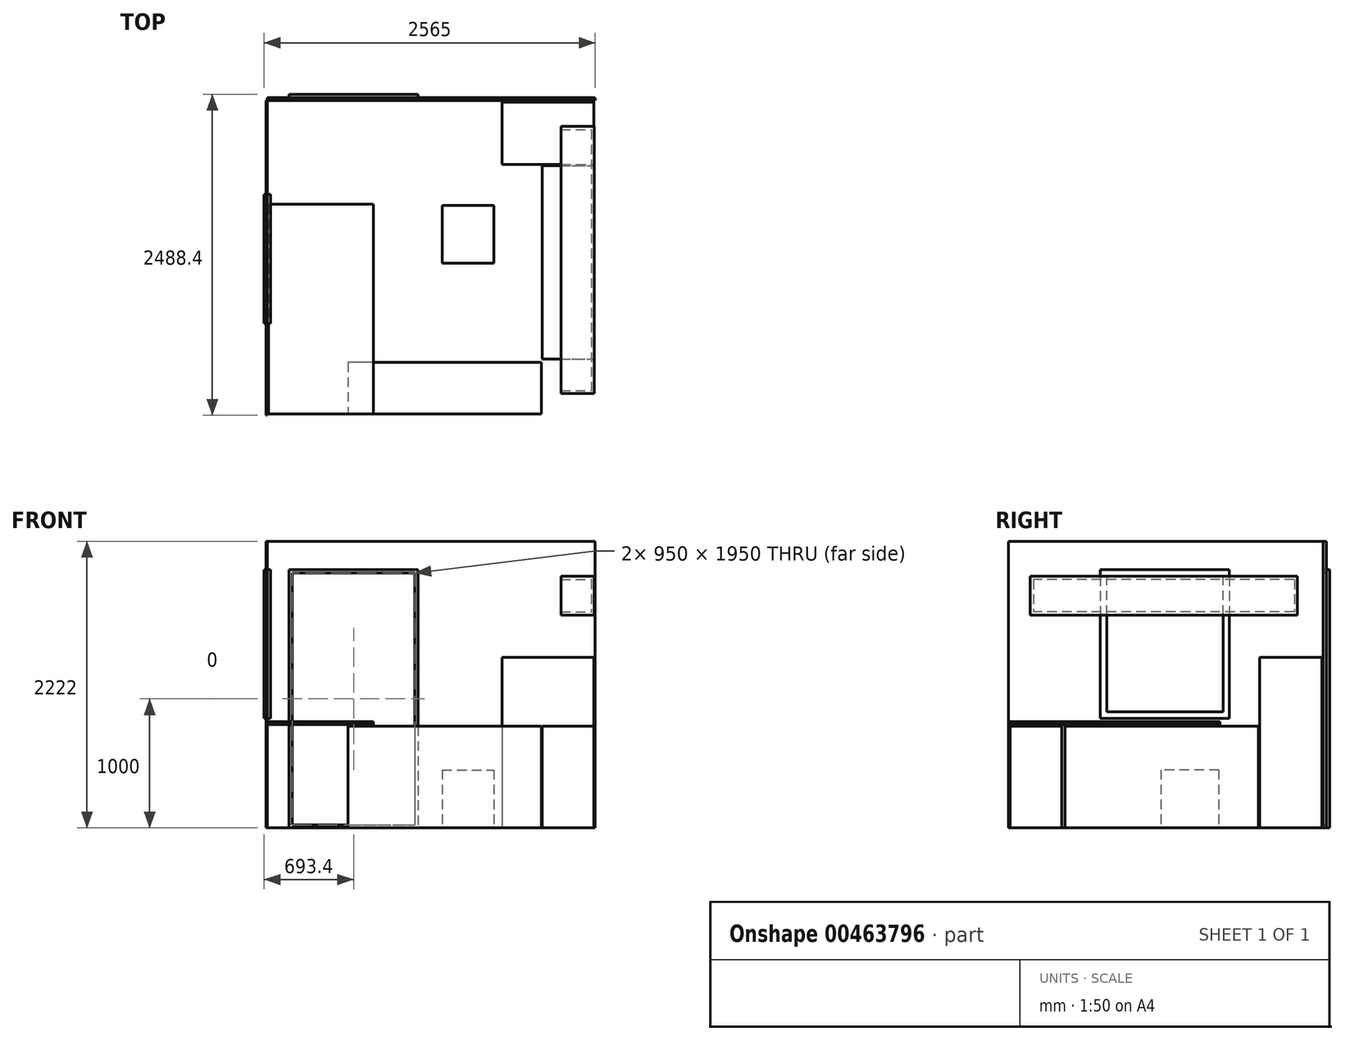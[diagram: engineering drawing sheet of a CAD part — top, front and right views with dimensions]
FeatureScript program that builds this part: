
annotation { "Feature Type Name" : "Feature", "Feature Type Description" : "" }
export const myFeature = defineFeature(function(context is Context, id is Id, definition is map)
    precondition{}
    {
        {
            var Q0;
            Q0=qCreatedBy(makeId("Top.planeOp"),FACE);
            var sketch = newSketch(context, id + "F0", { "sketchPlane" : qUnion([Q0])});
            skLineSegment(sketch, "E0.bottom", {"start": v(0, 0) * mm, "end": v(2540, 0) * mm});
            skLineSegment(sketch, "E0.top", {"start": v(0, 2438.4) * mm, "end": v(2540, 2438.4) * mm});
            skLineSegment(sketch, "E0.left", {"start": v(0, 0) * mm, "end": v(0, 2438.4) * mm});
            skLineSegment(sketch, "E0.right", {"start": v(2540, 0) * mm, "end": v(2540, 2438.4) * mm});
            skSolve(sketch);
        }
        {
            var Q0;
            Q0=qCreatedBy(makeId("Top.planeOp"),FACE);
            cPlane(context, id + "F1", {"entities" : qUnion([Q0]), "cplaneType" : CPlaneType.OFFSET, "offset" : 800 * mm, "width" : 150 * mm, "height" : 150 * mm});
        }
        {
            var Q0;
            Q0=qCreatedBy(makeId("Top.planeOp"),FACE);
            var sketch = newSketch(context, id + "F2", { "sketchPlane" : qUnion([Q0])});
            skLineSegment(sketch, "E1.bottom", {"start": v(1818.8, 2428.4) * mm, "end": v(2530, 2428.4) * mm});
            skLineSegment(sketch, "E1.top", {"start": v(1818.8, 1945.8) * mm, "end": v(2530, 1945.8) * mm});
            skLineSegment(sketch, "E1.left", {"start": v(1818.8, 2428.4) * mm, "end": v(1818.8, 1945.8) * mm});
            skLineSegment(sketch, "E1.right", {"start": v(2530, 2428.4) * mm, "end": v(2530, 1945.8) * mm});
            skSolve(sketch);
        }
        {
            var Q0;
            Q0=qCreatedBy(makeId("Top.planeOp"),FACE);
            var sketch = newSketch(context, id + "F3", { "sketchPlane" : qUnion([Q0])});
            skLineSegment(sketch, "E2.bottom", {"start": v(2130, 1935.8) * mm, "end": v(2530, 1935.8) * mm});
            skLineSegment(sketch, "E2.top", {"start": v(2130, 437.2) * mm, "end": v(2530, 437.2) * mm});
            skLineSegment(sketch, "E2.left", {"start": v(2130, 1935.8) * mm, "end": v(2130, 437.2) * mm});
            skLineSegment(sketch, "E2.right", {"start": v(2530, 1935.8) * mm, "end": v(2530, 437.2) * mm});
            skSolve(sketch);
        }
        {
            var Q0;
            Q0 = qSketchRegion(id + "F3", true);
            extrude(context, id + "F4", {"entities" : qUnion([Q0]), "depth" : (31 * 25.4) * mm});
        }
        {
            var Q0;
            Q0 = qSketchRegion(id + "F2", true);
            extrude(context, id + "F5", {"entities" : qUnion([Q0]), "depth" : 52 * 25.4 * mm});
        }
        {
            var Q0;
            Q0=makeQuery(id+"F0.imprint","IMPRINT",FACE,{"disambiguationData":[TD([[makeQuery(id+"F0.imprint","IMPRINT",EDGE,{"derivedFrom":sQuery(id+"F0.wireOp",EDGE,"E0.bottom")}),1.0]])]});
            var sketch = newSketch(context, id + "F6", { "sketchPlane" : qUnion([Q0])});
            skLineSegment(sketch, "E3.bottom", {"start": v(2125, 410) * mm, "end": v(626.4, 410) * mm});
            skLineSegment(sketch, "E3.top", {"start": v(2125, 10) * mm, "end": v(626.4, 10) * mm});
            skLineSegment(sketch, "E3.left", {"start": v(2125, 410) * mm, "end": v(2125, 10) * mm});
            skLineSegment(sketch, "E3.right", {"start": v(626.4, 410) * mm, "end": v(626.4, 10) * mm});
            skSolve(sketch);
        }
        {
            var Q0;
            Q0 = qSketchRegion(id + "F6", true);
            extrude(context, id + "F7", {"entities" : qUnion([Q0]), "depth" : 31 * 25.4 * mm});
        }
        {
            var Q0;
            Q0=qCreatedBy(id+"F1.planeOp",FACE);
            var sketch = newSketch(context, id + "F8", { "sketchPlane" : qUnion([Q0])});
            skLineSegment(sketch, "E4.bottom", {"start": v(10, 1635.6) * mm, "end": v(822.8, 1635.6) * mm});
            skLineSegment(sketch, "E4.top", {"start": v(10, 10) * mm, "end": v(822.8, 10) * mm});
            skLineSegment(sketch, "E4.left", {"start": v(10, 1635.6) * mm, "end": v(10, 10) * mm});
            skLineSegment(sketch, "E4.right", {"start": v(822.8, 1635.6) * mm, "end": v(822.8, 10) * mm});
            skSolve(sketch);
        }
        {
            var Q0;
            Q0 = qSketchRegion(id + "F8", true);
            extrude(context, id + "F9", {"entities" : qUnion([Q0]), "depth" : 25 * mm});
        }
        {
            var Q0;
            Q0=qCreatedBy(id+"F1.planeOp",FACE);
            cPlane(context, id + "F10", {"entities" : qUnion([Q0]), "cplaneType" : CPlaneType.OFFSET, "offset" : 850 * mm, "width" : 150 * mm, "height" : 150 * mm});
        }
        {
            var Q0;
            Q0=qCreatedBy(id+"F10.planeOp",FACE);
            var sketch = newSketch(context, id + "F11", { "sketchPlane" : qUnion([Q0])});
            skLineSegment(sketch, "E5.bottom", {"start": v(2275, 2238.4) * mm, "end": v(2535, 2238.4) * mm});
            skLineSegment(sketch, "E5.top", {"start": v(2275, 168.4) * mm, "end": v(2535, 168.4) * mm});
            skLineSegment(sketch, "E5.left", {"start": v(2275, 2238.4) * mm, "end": v(2275, 168.4) * mm});
            skLineSegment(sketch, "E5.right", {"start": v(2535, 2238.4) * mm, "end": v(2535, 168.4) * mm});
            skSolve(sketch);
        }
        {
            var Q0;
            Q0 = qSketchRegion(id + "F11", true);
            extrude(context, id + "F12", {"entities" : qUnion([Q0]), "depth" : 300 * mm});
        }
        {
            var Q0;
            Q0=makeQuery(id+"F12.opExtrude","SWEPT_FACE",FACE,{"disambiguationData":[OSD([sQuery(id+"F11.wireOp",EDGE,"E5.left")])]});
            shell(context, id + "F13", {"entities" : qUnion([Q0]), "thickness" : 25 * mm});
        }
        {
            var Q0;
            Q0=qCreatedBy(makeId("Top.planeOp"),FACE);
            var sketch = newSketch(context, id + "F14", { "sketchPlane" : qUnion([Q0])});
            skLineSegment(sketch, "E6.bottom", {"start": v(0, 2438.4) * mm, "end": v(-10, 2438.4) * mm});
            skLineSegment(sketch, "E6.top", {"start": v(0, 0) * mm, "end": v(-10, 0) * mm});
            skLineSegment(sketch, "E6.left", {"start": v(0, 2438.4) * mm, "end": v(0, 0) * mm});
            skLineSegment(sketch, "E6.right", {"start": v(-10, 2438.4) * mm, "end": v(-10, 0) * mm});
            skSolve(sketch);
        }
        {
            var Q0;
            Q0 = qSketchRegion(id + "F14", true);
            extrude(context, id + "F15", {"entities" : qUnion([Q0]), "depth" : 2222 * mm});
        }
        {
            var Q0;
            Q0=qCreatedBy(makeId("Right.planeOp"),FACE);
            var sketch = newSketch(context, id + "F16", { "sketchPlane" : qUnion([Q0])});
            skLineSegment(sketch, "E7.bottom", {"start": v(1711.2, 2000) * mm, "end": v(711.2, 2000) * mm});
            skLineSegment(sketch, "E7.top", {"start": v(1711.2, 850) * mm, "end": v(711.2, 850) * mm});
            skLineSegment(sketch, "E7.left", {"start": v(1711.2, 2000) * mm, "end": v(1711.2, 850) * mm});
            skLineSegment(sketch, "E7.right", {"start": v(711.2, 2000) * mm, "end": v(711.2, 850) * mm});
            skSolve(sketch);
        }
        {
            var Q0;
            Q0=qSketchRegion(id+"F16",true);
            extrude(context, id + "F17", {"entities" : qUnion([Q0]), "endBound" : BoundingType.SYMMETRIC, "depth" : 50 * mm});
        }
        {
            var Q0;
            Q0=makeQuery(id+"F17.opExtrude","CAP_FACE",FACE,{"disambiguationData":[OSD([sQuery(id+"F16.wireOp",EDGE,"E7.bottom"),sQuery(id+"F16.wireOp",EDGE,"E7.top"),sQuery(id+"F16.wireOp",EDGE,"E7.left"),sQuery(id+"F16.wireOp",EDGE,"E7.right")])],"isStart":false});
            var sketch = newSketch(context, id + "F18", { "sketchPlane" : qUnion([Q0])});
            skLineSegment(sketch, "E8.bottom", {"start": v(761.2, 1950) * mm, "end": v(1661.2, 1950) * mm});
            skLineSegment(sketch, "E8.top", {"start": v(761.2, 900) * mm, "end": v(1661.2, 900) * mm});
            skLineSegment(sketch, "E8.left", {"start": v(1661.2, 900) * mm, "end": v(1661.2, 1950) * mm});
            skLineSegment(sketch, "E8.right", {"start": v(761.2, 900) * mm, "end": v(761.2, 1950) * mm});
            skSolve(sketch);
        }
        {
            var Q0;
            Q0 = qSketchRegion(id + "F18", true);
            extrude(context, id + "F19", {"entities" : qUnion([Q0]), "operationType" : NewBodyOperationType.REMOVE, "endBound" : BoundingType.SYMMETRIC, "oppositeDirection" : true, "depth" : 100 * mm});
        }
        {
            var Q0;
            Q0=qCreatedBy(makeId("Top.planeOp"),FACE);
            var sketch = newSketch(context, id + "F20", { "sketchPlane" : qUnion([Q0])});
            skLineSegment(sketch, "E9.bottom", {"start": v(2540, 2438.4) * mm, "end": v(0, 2438.4) * mm});
            skLineSegment(sketch, "E9.top", {"start": v(2540, 2463.4) * mm, "end": v(0, 2463.4) * mm});
            skLineSegment(sketch, "E9.left", {"start": v(2540, 2438.4) * mm, "end": v(2540, 2463.4) * mm});
            skLineSegment(sketch, "E9.right", {"start": v(0, 2438.4) * mm, "end": v(0, 2463.4) * mm});
            skSolve(sketch);
        }
        {
            var Q0;
            Q0 = qSketchRegion(id + "F20", true);
            extrude(context, id + "F21", {"entities" : qUnion([Q0]), "operationType" : NewBodyOperationType.ADD, "depth" : 2222 * mm});
        }
        {
            var Q0;
            Q0=makeQuery(id+"F0.imprint","IMPRINT",FACE,{"disambiguationData":[TD([[makeQuery(id+"F0.imprint","IMPRINT",EDGE,{"derivedFrom":sQuery(id+"F0.wireOp",EDGE,"E0.bottom")}),1.0]])]});
            var sketch = newSketch(context, id + "F22", { "sketchPlane" : qUnion([Q0])});
            skLineSegment(sketch, "E10.bottom", {"start": v(168.4, 2488.4) * mm, "end": v(1168.4, 2488.4) * mm});
            skLineSegment(sketch, "E10.top", {"start": v(168.4, 2438.4) * mm, "end": v(1168.4, 2438.4) * mm});
            skLineSegment(sketch, "E10.left", {"start": v(168.4, 2488.4) * mm, "end": v(168.4, 2438.4) * mm});
            skLineSegment(sketch, "E10.right", {"start": v(1168.4, 2488.4) * mm, "end": v(1168.4, 2438.4) * mm});
            skSolve(sketch);
        }
        {
            var Q0;
            Q0 = qSketchRegion(id + "F22", true);
            extrude(context, id + "F23", {"entities" : qUnion([Q0]), "depth" : 2000 * mm});
        }
        {
            var Q0;
            Q0=makeQuery(id+"F23.opExtrude","SWEPT_FACE",FACE,{"disambiguationData":[OSD([sQuery(id+"F22.wireOp",EDGE,"E10.top")])]});
            var sketch = newSketch(context, id + "F24", { "sketchPlane" : qUnion([Q0])});
            skLineSegment(sketch, "E11.bottom", {"start": v(193.4, 1975) * mm, "end": v(1143.4, 1975) * mm});
            skLineSegment(sketch, "E11.top", {"start": v(193.4, 25) * mm, "end": v(1143.4, 25) * mm});
            skLineSegment(sketch, "E11.left", {"start": v(193.4, 1975) * mm, "end": v(193.4, 25) * mm});
            skLineSegment(sketch, "E11.right", {"start": v(1143.4, 1975) * mm, "end": v(1143.4, 25) * mm});
            skSolve(sketch);
        }
        {
            var Q0;
            Q0=makeQuery(id+"F24.imprint","IMPRINT",FACE,{"disambiguationData":[TD([[makeQuery(id+"F24.imprint","IMPRINT",EDGE,{"derivedFrom":sQuery(id+"F24.wireOp",EDGE,"E11.bottom")}),-1.0]])]});
            extrude(context, id + "F25", {"entities" : qUnion([Q0]), "operationType" : NewBodyOperationType.REMOVE, "endBound" : BoundingType.SYMMETRIC, "oppositeDirection" : true, "depth" : 100 * mm});
        }
        {
            var Q0;
            Q0=makeQuery(id+"F0.imprint","IMPRINT",FACE,{"disambiguationData":[TD([[makeQuery(id+"F0.imprint","IMPRINT",EDGE,{"derivedFrom":sQuery(id+"F0.wireOp",EDGE,"E0.bottom")}),1.0]])]});
            var sketch = newSketch(context, id + "F26", { "sketchPlane" : qUnion([Q0])});
            skLineSegment(sketch, "E12.bottom", {"start": v(1355, 1628.4) * mm, "end": v(1755, 1628.4) * mm});
            skLineSegment(sketch, "E12.top", {"start": v(1355, 1178.4) * mm, "end": v(1755, 1178.4) * mm});
            skLineSegment(sketch, "E12.left", {"start": v(1355, 1628.4) * mm, "end": v(1355, 1178.4) * mm});
            skLineSegment(sketch, "E12.right", {"start": v(1755, 1628.4) * mm, "end": v(1755, 1178.4) * mm});
            skSolve(sketch);
        }
        {
            var Q0;
            Q0=makeQuery(id+"F26.imprint","IMPRINT",FACE,{"disambiguationData":[TD([[makeQuery(id+"F26.imprint","IMPRINT",EDGE,{"derivedFrom":sQuery(id+"F26.wireOp",EDGE,"E12.bottom")}),-1.0]])]});
            extrude(context, id + "F27", {"entities" : qUnion([Q0]), "depth" : 450 * mm});
        }
    });
